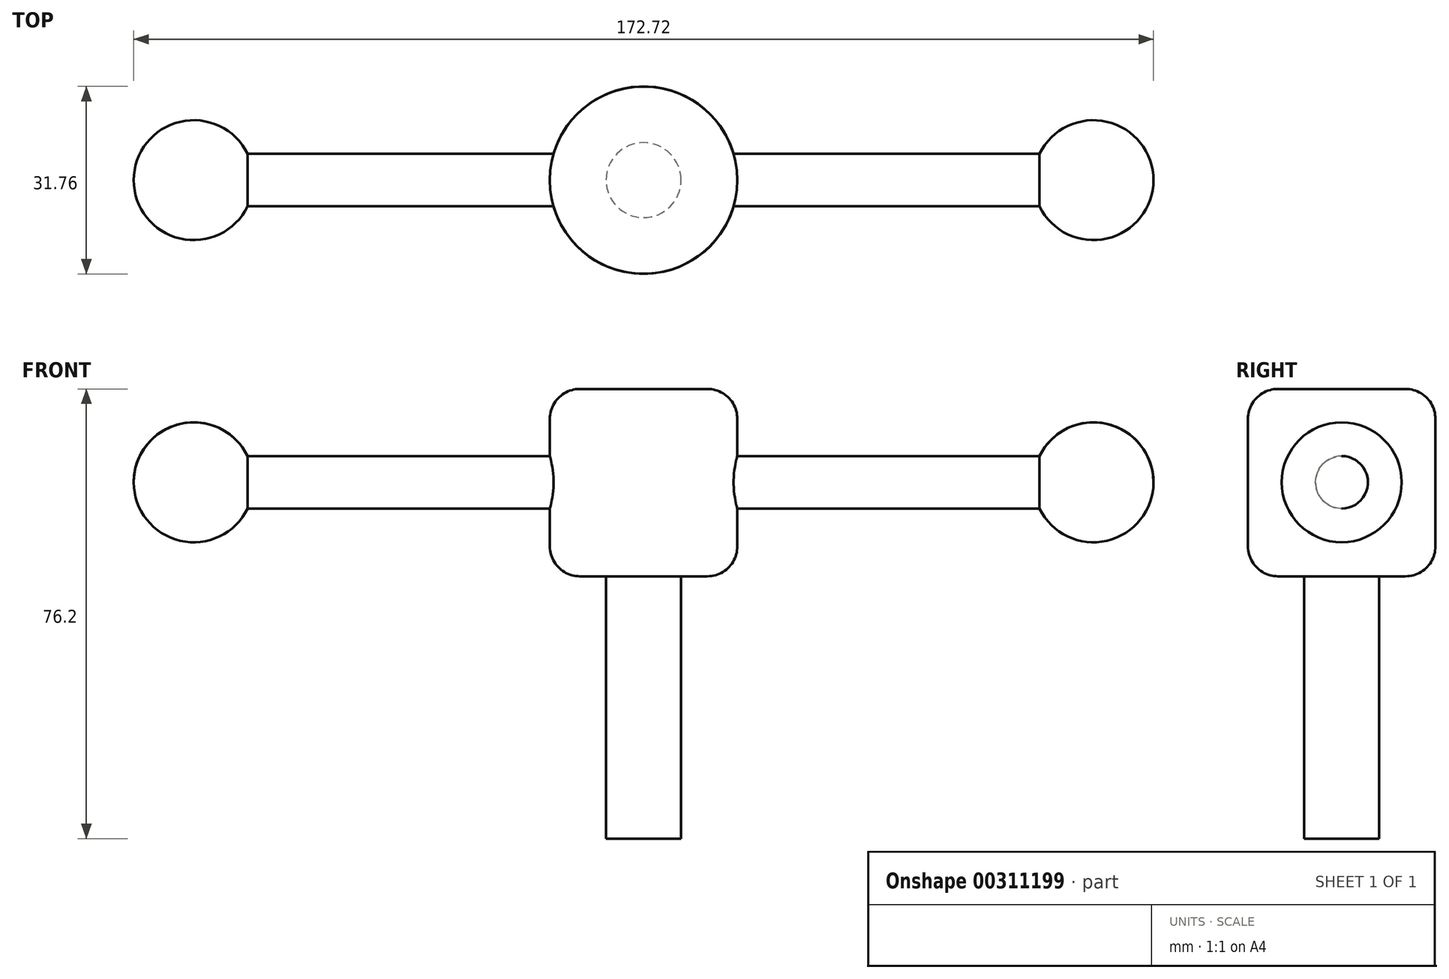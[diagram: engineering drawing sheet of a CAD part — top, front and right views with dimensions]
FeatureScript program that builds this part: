
annotation { "Feature Type Name" : "Feature", "Feature Type Description" : "" }
export const myFeature = defineFeature(function(context is Context, id is Id, definition is map)
    precondition{}
    {
        {
            var Q0;
            Q0=qCreatedBy(makeId("Top.planeOp"),FACE);
            var sketch = newSketch(context, id + "F0", { "sketchPlane" : qUnion([Q0])});
            skCircle(sketch, "E0", {"center": v(0, 0) * mm, "radius": 15.88 * mm});
            skSolve(sketch);
        }
        {
            var Q0;
            Q0 = qSketchRegion(id + "F0", true);
            extrude(context, id + "F1", {"entities" : qUnion([Q0]), "depth" : 31.75 * mm});
        }
        {
            var Q0;
            Q0=makeQuery(id+"F1.opExtrude","CAP_FACE",FACE,{"disambiguationData":[OSD([sQuery(id+"F0.wireOp",EDGE,"E0")])],"isStart":true});
            var sketch = newSketch(context, id + "F2", { "sketchPlane" : qUnion([Q0])});
            skCircle(sketch, "E1", {"center": v(0, 0) * mm, "radius": 6.35 * mm});
            skSolve(sketch);
        }
        {
            var Q0;
            Q0 = qSketchRegion(id + "F2", true);
            extrude(context, id + "F3", {"entities" : qUnion([Q0]), "operationType" : NewBodyOperationType.ADD, "depth" : 44.45 * mm});
        }
        {
            var Q0;
            Q0=qCreatedBy(makeId("Right.planeOp"),FACE);
            var sketch = newSketch(context, id + "F4", { "sketchPlane" : qUnion([Q0])});
            skLineSegment(sketch, "E2", {"start": v(-15.88, 0) * mm, "end": v(-15.88, 31.75) * mm});
            skLineSegment(sketch, "E3", {"start": v(15.88, 31.75) * mm, "end": v(15.88, 0) * mm});
            skLineSegment(sketch, "E4", {"start": v(0, 0) * mm, "end": v(0, 31.85) * mm, "construction": true});
            skCircle(sketch, "E5", {"center": v(0, 15.93) * mm, "radius": 4.45 * mm});
            skSolve(sketch);
        }
        {
            var Q0;
            Q0 = qSketchRegion(id + "F4", true);
            extrude(context, id + "F5", {"entities" : qUnion([Q0]), "operationType" : NewBodyOperationType.ADD, "endBound" : BoundingType.SYMMETRIC, "depth" : 152.4 * mm});
        }
        {
            var Q0;
            Q0=qCreatedBy(makeId("Front.planeOp"),FACE);
            var sketch = newSketch(context, id + "F6", { "sketchPlane" : qUnion([Q0])});
            skLineSegment(sketch, "E6", {"start": v(-76.2, 20.37) * mm, "end": v(-15.87, 20.37) * mm});
            skLineSegment(sketch, "E7", {"start": v(-15.87, 11.48) * mm, "end": v(-76.2, 11.48) * mm});
            skLineSegment(sketch, "E8", {"start": v(-76.2, 11.48) * mm, "end": v(-76.2, 20.37) * mm, "construction": true});
            skArc(sketch, "E9", {"start": v(-67.06, 20.37) * mm, "mid": v(-78.48, 25.83) * mm, "end": v(-86.36, 15.93) * mm});
            skLineSegment(sketch, "E10", {"start": v(-76.2, 15.93) * mm, "end": v(-86.36, 15.93) * mm, "construction": true});
            skLineSegment(sketch, "E11", {"start": v(-76.2, 15.93) * mm, "end": v(-86.36, 15.93) * mm});
            skLineSegment(sketch, "E12", {"start": v(-76.2, 15.93) * mm, "end": v(-76.2, 20.37) * mm});
            skSolve(sketch);
        }
        {
            var Q0;
            Q0 = qSketchRegion(id + "F6", true);
            var Q1;
            Q1=sQuery(id+"F6.wireOp",EDGE,"E11");
            revolve(context, id + "F7", {"operationType" : NewBodyOperationType.ADD, "entities" : qUnion([Q0]), "axis" : qUnion([Q1]), "revolveType" : RevolveType.FULL});
        }
        {
            var Q0;
            Q0=qCreatedBy(makeId("Front.planeOp"),FACE);
            var sketch = newSketch(context, id + "F8", { "sketchPlane" : qUnion([Q0])});
            skLineSegment(sketch, "E13", {"start": v(15.88, 20.37) * mm, "end": v(76.2, 20.37) * mm});
            skLineSegment(sketch, "E14", {"start": v(76.2, 11.48) * mm, "end": v(15.88, 11.48) * mm});
            skLineSegment(sketch, "E15", {"start": v(76.2, 20.37) * mm, "end": v(76.2, 11.48) * mm, "construction": true});
            skArc(sketch, "E16", {"start": v(86.36, 15.93) * mm, "mid": v(78.48, 25.83) * mm, "end": v(67.06, 20.37) * mm});
            skLineSegment(sketch, "E17", {"start": v(76.2, 15.93) * mm, "end": v(86.36, 15.93) * mm, "construction": true});
            skLineSegment(sketch, "E18", {"start": v(76.2, 15.93) * mm, "end": v(86.36, 15.93) * mm});
            skLineSegment(sketch, "E19", {"start": v(76.2, 15.93) * mm, "end": v(76.2, 20.37) * mm});
            skSolve(sketch);
        }
        {
            var Q0;
            Q0 = qSketchRegion(id + "F8", true);
            var Q1;
            Q1=sQuery(id+"F8.wireOp",EDGE,"E18");
            revolve(context, id + "F9", {"operationType" : NewBodyOperationType.ADD, "entities" : qUnion([Q0]), "axis" : qUnion([Q1]), "revolveType" : RevolveType.FULL});
        }
        {
            var Q0;
            Q0=makeQuery(id+"F1.opExtrude","CAP_EDGE",EDGE,{"disambiguationData":[OSD([sQuery(id+"F0.wireOp",EDGE,"E0")])],"isStart":false});
            var Q1;
            Q1=makeQuery(id+"F1.opExtrude","CAP_EDGE",EDGE,{"disambiguationData":[OSD([sQuery(id+"F0.wireOp",EDGE,"E0")])],"isStart":true});
            fillet(context, id + "F10", {"entities" : qUnion([Q0, Q1]), "radius" : 5.08 * mm, "tangentPropagation" : true, "allowEdgeOverflow" : false});
        }
    });
